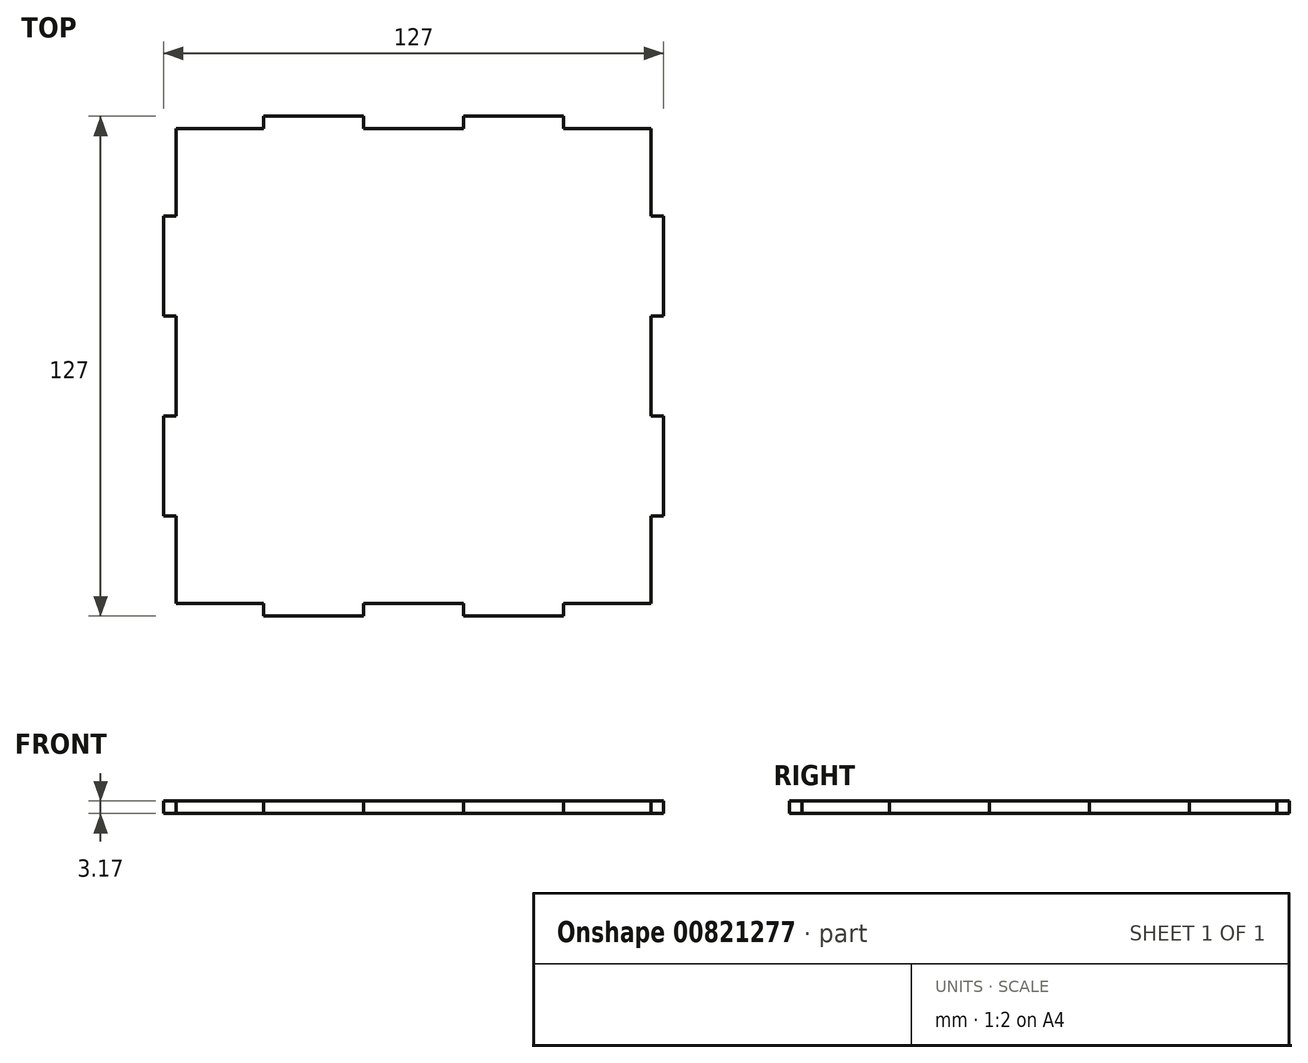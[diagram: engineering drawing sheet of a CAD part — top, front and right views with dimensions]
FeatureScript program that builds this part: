
annotation { "Feature Type Name" : "Feature", "Feature Type Description" : "" }
export const myFeature = defineFeature(function(context is Context, id is Id, definition is map)
    precondition{}
    {
        {
            var Q0;
            Q0=qCreatedBy(makeId("Top.planeOp"),FACE);
            var sketch = newSketch(context, id + "F0", { "sketchPlane" : qUnion([Q0])});
            skLineSegment(sketch, "E0.bottom", {"start": v(-63.5, 63.5) * mm, "end": v(63.5, 63.5) * mm});
            skLineSegment(sketch, "E0.top", {"start": v(-63.5, -63.5) * mm, "end": v(63.5, -63.5) * mm});
            skLineSegment(sketch, "E0.left", {"start": v(-63.5, 63.5) * mm, "end": v(-63.5, -63.5) * mm});
            skLineSegment(sketch, "E0.right", {"start": v(63.5, 63.5) * mm, "end": v(63.5, -63.5) * mm});
            skPoint(sketch, "E0.middle", {"position": v(0, 0) * mm});
            skLineSegment(sketch, "E1", {"start": v(-38.1, 63.5) * mm, "end": v(-38.1, -63.5) * mm});
            skLineSegment(sketch, "E2", {"start": v(-63.5, -38.1) * mm, "end": v(63.5, -38.1) * mm});
            skLineSegment(sketch, "E3.1.0.0", {"start": v(-12.7, 63.5) * mm, "end": v(-12.7, -63.5) * mm});
            skLineSegment(sketch, "E3.2.0.0", {"start": v(12.7, 63.5) * mm, "end": v(12.7, -63.5) * mm});
            skLineSegment(sketch, "E3.3.0.0", {"start": v(38.1, 63.5) * mm, "end": v(38.1, -63.5) * mm});
            skLineSegment(sketch, "E3.direction1", {"start": v(-38.1, -63.5) * mm, "end": v(-12.7, -63.5) * mm, "construction": true});
            skLineSegment(sketch, "E4.0.1.0", {"start": v(-63.5, -12.7) * mm, "end": v(63.5, -12.7) * mm});
            skLineSegment(sketch, "E4.0.2.0", {"start": v(-63.5, 12.7) * mm, "end": v(63.5, 12.7) * mm});
            skLineSegment(sketch, "E4.0.3.0", {"start": v(-63.5, 38.1) * mm, "end": v(63.5, 38.1) * mm});
            skLineSegment(sketch, "E4.1.0.0", {"start": v(-38.1, -38.1) * mm, "end": v(63.5, -38.1) * mm});
            skLineSegment(sketch, "E4.1.1.0", {"start": v(-38.1, -12.7) * mm, "end": v(63.5, -12.7) * mm});
            skLineSegment(sketch, "E4.1.2.0", {"start": v(-38.1, 12.7) * mm, "end": v(63.5, 12.7) * mm});
            skLineSegment(sketch, "E4.1.3.0", {"start": v(-38.1, 38.1) * mm, "end": v(63.5, 38.1) * mm});
            skLineSegment(sketch, "E4.2.0.0", {"start": v(-12.7, -38.1) * mm, "end": v(63.5, -38.1) * mm});
            skLineSegment(sketch, "E4.2.1.0", {"start": v(-12.7, -12.7) * mm, "end": v(63.5, -12.7) * mm});
            skLineSegment(sketch, "E4.2.2.0", {"start": v(-12.7, 12.7) * mm, "end": v(63.5, 12.7) * mm});
            skLineSegment(sketch, "E4.2.3.0", {"start": v(-12.7, 38.1) * mm, "end": v(63.5, 38.1) * mm});
            skLineSegment(sketch, "E4.direction1", {"start": v(-63.5, -38.1) * mm, "end": v(-38.1, -38.1) * mm, "construction": true});
            skLineSegment(sketch, "E4.direction2", {"start": v(-63.5, -38.1) * mm, "end": v(-63.5, -12.7) * mm, "construction": true});
            skLineSegment(sketch, "E5", {"start": v(-63.5, -60.33) * mm, "end": v(63.5, -60.32) * mm});
            skLineSegment(sketch, "E6", {"start": v(-60.33, 63.5) * mm, "end": v(-60.33, -63.5) * mm});
            skLineSegment(sketch, "E7", {"start": v(-63.5, 60.33) * mm, "end": v(63.5, 60.33) * mm});
            skLineSegment(sketch, "E8", {"start": v(60.32, 63.5) * mm, "end": v(60.32, -63.5) * mm});
            skSolve(sketch);
        }
        {
            var Q0;
            {var subQ0=sQuery(id+"F0.wireOp",EDGE,"E7");var subQ1=sQuery(id+"F0.wireOp",EDGE,"E1");var subQ2=makeQuery(id+"F0.imprint","INTERSECT",VERTEX,{"derivedFrom":[subQ1,subQ0]});Q0=makeQuery(id+"F0.imprint","IMPRINT",FACE,{"disambiguationData":[TD([[makeQuery(id+"F0.imprint","IMPRINT",EDGE,{"disambiguationData":[TD([[subQ2,-1.0]])],"derivedFrom":subQ1}),-1.0]])]});}
            var Q1;
            {var subQ0=sQuery(id+"F0.wireOp",EDGE,"E7");var subQ1=sQuery(id+"F0.wireOp",EDGE,"E1");var subQ2=makeQuery(id+"F0.imprint","INTERSECT",VERTEX,{"derivedFrom":[subQ1,subQ0]});Q1=makeQuery(id+"F0.imprint","IMPRINT",FACE,{"disambiguationData":[TD([[makeQuery(id+"F0.imprint","IMPRINT",EDGE,{"disambiguationData":[TD([[subQ2,-1.0]])],"derivedFrom":subQ1}),1.0]])]});}
            var Q2;
            {var subQ0=sQuery(id+"F0.wireOp",EDGE,"E7");var subQ1=sQuery(id+"F0.wireOp",EDGE,"E3.2.0.0");var subQ2=makeQuery(id+"F0.imprint","INTERSECT",VERTEX,{"derivedFrom":[subQ1,subQ0]});Q2=makeQuery(id+"F0.imprint","IMPRINT",FACE,{"disambiguationData":[TD([[makeQuery(id+"F0.imprint","IMPRINT",EDGE,{"disambiguationData":[TD([[subQ2,-1.0]])],"derivedFrom":subQ1}),1.0]])]});}
            var Q3;
            {var subQ0=sQuery(id+"F0.wireOp",EDGE,"E7");var subQ1=sQuery(id+"F0.wireOp",EDGE,"E3.3.0.0");var subQ2=makeQuery(id+"F0.imprint","INTERSECT",VERTEX,{"derivedFrom":[subQ1,subQ0]});Q3=makeQuery(id+"F0.imprint","IMPRINT",FACE,{"disambiguationData":[TD([[makeQuery(id+"F0.imprint","IMPRINT",EDGE,{"disambiguationData":[TD([[subQ2,-1.0]])],"derivedFrom":subQ1}),1.0]])]});}
            var Q4;
            {var subQ0=sQuery(id+"F0.wireOp",EDGE,"E4.0.2.0");var subQ1=sQuery(id+"F0.wireOp",EDGE,"E3.3.0.0");var subQ2=makeQuery(id+"F0.imprint","INTERSECT",VERTEX,{"derivedFrom":[subQ1,subQ0]});Q4=makeQuery(id+"F0.imprint","IMPRINT",FACE,{"disambiguationData":[TD([[makeQuery(id+"F0.imprint","IMPRINT",EDGE,{"disambiguationData":[TD([[subQ2,1.0]])],"derivedFrom":subQ1}),1.0]])]});}
            var Q5;
            {var subQ0=sQuery(id+"F0.wireOp",EDGE,"E4.0.2.0");var subQ1=sQuery(id+"F0.wireOp",EDGE,"E3.2.0.0");var subQ2=makeQuery(id+"F0.imprint","INTERSECT",VERTEX,{"derivedFrom":[subQ1,subQ0]});Q5=makeQuery(id+"F0.imprint","IMPRINT",FACE,{"disambiguationData":[TD([[makeQuery(id+"F0.imprint","IMPRINT",EDGE,{"disambiguationData":[TD([[subQ2,1.0]])],"derivedFrom":subQ1}),1.0]])]});}
            var Q6;
            {var subQ0=sQuery(id+"F0.wireOp",EDGE,"E4.0.2.0");var subQ1=sQuery(id+"F0.wireOp",EDGE,"E3.1.0.0");var subQ2=makeQuery(id+"F0.imprint","INTERSECT",VERTEX,{"derivedFrom":[subQ1,subQ0]});Q6=makeQuery(id+"F0.imprint","IMPRINT",FACE,{"disambiguationData":[TD([[makeQuery(id+"F0.imprint","IMPRINT",EDGE,{"disambiguationData":[TD([[subQ2,1.0]])],"derivedFrom":subQ1}),1.0]])]});}
            var Q7;
            {var subQ0=sQuery(id+"F0.wireOp",EDGE,"E4.0.2.0");var subQ1=sQuery(id+"F0.wireOp",EDGE,"E1");var subQ2=makeQuery(id+"F0.imprint","INTERSECT",VERTEX,{"derivedFrom":[subQ1,subQ0]});Q7=makeQuery(id+"F0.imprint","IMPRINT",FACE,{"disambiguationData":[TD([[makeQuery(id+"F0.imprint","IMPRINT",EDGE,{"disambiguationData":[TD([[subQ2,1.0]])],"derivedFrom":subQ1}),1.0]])]});}
            var Q8;
            {var subQ0=sQuery(id+"F0.wireOp",EDGE,"E4.0.2.0");var subQ1=sQuery(id+"F0.wireOp",EDGE,"E1");var subQ2=makeQuery(id+"F0.imprint","INTERSECT",VERTEX,{"derivedFrom":[subQ1,subQ0]});Q8=makeQuery(id+"F0.imprint","IMPRINT",FACE,{"disambiguationData":[TD([[makeQuery(id+"F0.imprint","IMPRINT",EDGE,{"disambiguationData":[TD([[subQ2,1.0]])],"derivedFrom":subQ1}),-1.0]])]});}
            var Q9;
            {var subQ0=sQuery(id+"F0.wireOp",EDGE,"E4.0.2.0");var subQ1=sQuery(id+"F0.wireOp",EDGE,"E1");var subQ2=makeQuery(id+"F0.imprint","INTERSECT",VERTEX,{"derivedFrom":[subQ1,subQ0]});Q9=makeQuery(id+"F0.imprint","IMPRINT",FACE,{"disambiguationData":[TD([[makeQuery(id+"F0.imprint","IMPRINT",EDGE,{"disambiguationData":[TD([[subQ2,-1.0]])],"derivedFrom":subQ1}),-1.0]])]});}
            var Q10;
            {var subQ0=sQuery(id+"F0.wireOp",EDGE,"E4.0.2.0");var subQ1=sQuery(id+"F0.wireOp",EDGE,"E1");var subQ2=makeQuery(id+"F0.imprint","INTERSECT",VERTEX,{"derivedFrom":[subQ1,subQ0]});Q10=makeQuery(id+"F0.imprint","IMPRINT",FACE,{"disambiguationData":[TD([[makeQuery(id+"F0.imprint","IMPRINT",EDGE,{"disambiguationData":[TD([[subQ2,-1.0]])],"derivedFrom":subQ1}),1.0]])]});}
            var Q11;
            {var subQ0=sQuery(id+"F0.wireOp",EDGE,"E4.0.1.0");var subQ1=sQuery(id+"F0.wireOp",EDGE,"E3.1.0.0");var subQ2=makeQuery(id+"F0.imprint","INTERSECT",VERTEX,{"derivedFrom":[subQ1,subQ0]});Q11=makeQuery(id+"F0.imprint","IMPRINT",FACE,{"disambiguationData":[TD([[makeQuery(id+"F0.imprint","IMPRINT",EDGE,{"disambiguationData":[TD([[subQ2,1.0]])],"derivedFrom":subQ1}),1.0]])]});}
            var Q12;
            {var subQ0=sQuery(id+"F0.wireOp",EDGE,"E4.0.1.0");var subQ1=sQuery(id+"F0.wireOp",EDGE,"E3.2.0.0");var subQ2=makeQuery(id+"F0.imprint","INTERSECT",VERTEX,{"derivedFrom":[subQ1,subQ0]});Q12=makeQuery(id+"F0.imprint","IMPRINT",FACE,{"disambiguationData":[TD([[makeQuery(id+"F0.imprint","IMPRINT",EDGE,{"disambiguationData":[TD([[subQ2,1.0]])],"derivedFrom":subQ1}),1.0]])]});}
            var Q13;
            {var subQ0=sQuery(id+"F0.wireOp",EDGE,"E4.0.1.0");var subQ1=sQuery(id+"F0.wireOp",EDGE,"E3.3.0.0");var subQ2=makeQuery(id+"F0.imprint","INTERSECT",VERTEX,{"derivedFrom":[subQ1,subQ0]});Q13=makeQuery(id+"F0.imprint","IMPRINT",FACE,{"disambiguationData":[TD([[makeQuery(id+"F0.imprint","IMPRINT",EDGE,{"disambiguationData":[TD([[subQ2,1.0]])],"derivedFrom":subQ1}),1.0]])]});}
            var Q14;
            {var subQ0=sQuery(id+"F0.wireOp",EDGE,"E3.3.0.0");var subQ1=sQuery(id+"F0.wireOp",EDGE,"E2");var subQ2=makeQuery(id+"F0.imprint","INTERSECT",VERTEX,{"derivedFrom":[subQ1,subQ0]});Q14=makeQuery(id+"F0.imprint","IMPRINT",FACE,{"disambiguationData":[TD([[makeQuery(id+"F0.imprint","IMPRINT",EDGE,{"disambiguationData":[TD([[subQ2,-1.0]])],"derivedFrom":subQ1}),1.0]])]});}
            var Q15;
            {var subQ0=sQuery(id+"F0.wireOp",EDGE,"E3.2.0.0");var subQ1=sQuery(id+"F0.wireOp",EDGE,"E2");var subQ2=makeQuery(id+"F0.imprint","INTERSECT",VERTEX,{"derivedFrom":[subQ1,subQ0]});Q15=makeQuery(id+"F0.imprint","IMPRINT",FACE,{"disambiguationData":[TD([[makeQuery(id+"F0.imprint","IMPRINT",EDGE,{"disambiguationData":[TD([[subQ2,-1.0]])],"derivedFrom":subQ1}),1.0]])]});}
            var Q16;
            {var subQ0=sQuery(id+"F0.wireOp",EDGE,"E3.1.0.0");var subQ1=sQuery(id+"F0.wireOp",EDGE,"E2");var subQ2=makeQuery(id+"F0.imprint","INTERSECT",VERTEX,{"derivedFrom":[subQ1,subQ0]});Q16=makeQuery(id+"F0.imprint","IMPRINT",FACE,{"disambiguationData":[TD([[makeQuery(id+"F0.imprint","IMPRINT",EDGE,{"disambiguationData":[TD([[subQ2,-1.0]])],"derivedFrom":subQ1}),1.0]])]});}
            var Q17;
            {var subQ0=sQuery(id+"F0.wireOp",EDGE,"E4.0.1.0");var subQ1=sQuery(id+"F0.wireOp",EDGE,"E1");var subQ2=makeQuery(id+"F0.imprint","INTERSECT",VERTEX,{"derivedFrom":[subQ1,subQ0]});Q17=makeQuery(id+"F0.imprint","IMPRINT",FACE,{"disambiguationData":[TD([[makeQuery(id+"F0.imprint","IMPRINT",EDGE,{"disambiguationData":[TD([[subQ2,-1.0]])],"derivedFrom":subQ1}),1.0]])]});}
            var Q18;
            {var subQ0=sQuery(id+"F0.wireOp",EDGE,"E4.0.1.0");var subQ1=sQuery(id+"F0.wireOp",EDGE,"E1");var subQ2=makeQuery(id+"F0.imprint","INTERSECT",VERTEX,{"derivedFrom":[subQ1,subQ0]});Q18=makeQuery(id+"F0.imprint","IMPRINT",FACE,{"disambiguationData":[TD([[makeQuery(id+"F0.imprint","IMPRINT",EDGE,{"disambiguationData":[TD([[subQ2,-1.0]])],"derivedFrom":subQ1}),-1.0]])]});}
            var Q19;
            {var subQ0=sQuery(id+"F0.wireOp",EDGE,"E5");var subQ1=sQuery(id+"F0.wireOp",EDGE,"E1");var subQ2=makeQuery(id+"F0.imprint","INTERSECT",VERTEX,{"derivedFrom":[subQ1,subQ0]});Q19=makeQuery(id+"F0.imprint","IMPRINT",FACE,{"disambiguationData":[TD([[makeQuery(id+"F0.imprint","IMPRINT",EDGE,{"disambiguationData":[TD([[subQ2,1.0]])],"derivedFrom":subQ1}),-1.0]])]});}
            var Q20;
            {var subQ0=sQuery(id+"F0.wireOp",EDGE,"E5");var subQ1=sQuery(id+"F0.wireOp",EDGE,"E1");var subQ2=makeQuery(id+"F0.imprint","INTERSECT",VERTEX,{"derivedFrom":[subQ1,subQ0]});Q20=makeQuery(id+"F0.imprint","IMPRINT",FACE,{"disambiguationData":[TD([[makeQuery(id+"F0.imprint","IMPRINT",EDGE,{"disambiguationData":[TD([[subQ2,1.0]])],"derivedFrom":subQ1}),1.0]])]});}
            var Q21;
            {var subQ0=sQuery(id+"F0.wireOp",EDGE,"E3.2.0.0");var subQ1=sQuery(id+"F0.wireOp",EDGE,"E2");var subQ2=makeQuery(id+"F0.imprint","INTERSECT",VERTEX,{"derivedFrom":[subQ1,subQ0]});Q21=makeQuery(id+"F0.imprint","IMPRINT",FACE,{"disambiguationData":[TD([[makeQuery(id+"F0.imprint","IMPRINT",EDGE,{"disambiguationData":[TD([[subQ2,-1.0]])],"derivedFrom":subQ1}),-1.0]])]});}
            var Q22;
            {var subQ0=sQuery(id+"F0.wireOp",EDGE,"E3.3.0.0");var subQ1=sQuery(id+"F0.wireOp",EDGE,"E2");var subQ2=makeQuery(id+"F0.imprint","INTERSECT",VERTEX,{"derivedFrom":[subQ1,subQ0]});Q22=makeQuery(id+"F0.imprint","IMPRINT",FACE,{"disambiguationData":[TD([[makeQuery(id+"F0.imprint","IMPRINT",EDGE,{"disambiguationData":[TD([[subQ2,-1.0]])],"derivedFrom":subQ1}),-1.0]])]});}
            var Q23;
            {var subQ0=sQuery(id+"F0.wireOp",EDGE,"E7");var subQ1=sQuery(id+"F0.wireOp",EDGE,"E3.1.0.0");var subQ2=makeQuery(id+"F0.imprint","INTERSECT",VERTEX,{"derivedFrom":[subQ1,subQ0]});Q23=makeQuery(id+"F0.imprint","IMPRINT",FACE,{"disambiguationData":[TD([[makeQuery(id+"F0.imprint","IMPRINT",EDGE,{"disambiguationData":[TD([[subQ2,-1.0]])],"derivedFrom":subQ1}),1.0]])]});}
            var Q24;
            {var subQ0=sQuery(id+"F0.wireOp",EDGE,"E3.1.0.0");var subQ1=sQuery(id+"F0.wireOp",EDGE,"E2");var subQ2=makeQuery(id+"F0.imprint","INTERSECT",VERTEX,{"derivedFrom":[subQ1,subQ0]});Q24=makeQuery(id+"F0.imprint","IMPRINT",FACE,{"disambiguationData":[TD([[makeQuery(id+"F0.imprint","IMPRINT",EDGE,{"disambiguationData":[TD([[subQ2,-1.0]])],"derivedFrom":subQ1}),-1.0]])]});}
            var Q25;
            {var subQ0=sQuery(id+"F0.wireOp",EDGE,"E3.1.0.0");var subQ1=sQuery(id+"F0.wireOp",EDGE,"E0.top");var subQ2=makeQuery(id+"F0.imprint","INTERSECT",VERTEX,{"derivedFrom":[subQ1,subQ0]});Q25=makeQuery(id+"F0.imprint","IMPRINT",FACE,{"disambiguationData":[TD([[makeQuery(id+"F0.imprint","IMPRINT",EDGE,{"disambiguationData":[TD([[subQ2,1.0]])],"derivedFrom":subQ1}),1.0]])]});}
            var Q26;
            {var subQ0=sQuery(id+"F0.wireOp",EDGE,"E4.0.1.0");var subQ1=sQuery(id+"F0.wireOp",EDGE,"E0.left");var subQ2=makeQuery(id+"F0.imprint","INTERSECT",VERTEX,{"derivedFrom":[subQ1,subQ0]});Q26=makeQuery(id+"F0.imprint","IMPRINT",FACE,{"disambiguationData":[TD([[makeQuery(id+"F0.imprint","IMPRINT",EDGE,{"disambiguationData":[TD([[subQ2,-1.0]])],"derivedFrom":subQ1}),1.0]])]});}
            var Q27;
            {var subQ0=sQuery(id+"F0.wireOp",EDGE,"E4.0.2.0");var subQ1=sQuery(id+"F0.wireOp",EDGE,"E0.left");var subQ2=makeQuery(id+"F0.imprint","INTERSECT",VERTEX,{"derivedFrom":[subQ1,subQ0]});Q27=makeQuery(id+"F0.imprint","IMPRINT",FACE,{"disambiguationData":[TD([[makeQuery(id+"F0.imprint","IMPRINT",EDGE,{"disambiguationData":[TD([[subQ2,1.0]])],"derivedFrom":subQ1}),1.0]])]});}
            var Q28;
            {var subQ0=sQuery(id+"F0.wireOp",EDGE,"E1");var subQ1=sQuery(id+"F0.wireOp",EDGE,"E0.bottom");var subQ2=makeQuery(id+"F0.imprint","INTERSECT",VERTEX,{"derivedFrom":[subQ1,subQ0]});Q28=makeQuery(id+"F0.imprint","IMPRINT",FACE,{"disambiguationData":[TD([[makeQuery(id+"F0.imprint","IMPRINT",EDGE,{"disambiguationData":[TD([[subQ2,-1.0]])],"derivedFrom":subQ1}),-1.0]])]});}
            var Q29;
            {var subQ0=sQuery(id+"F0.wireOp",EDGE,"E3.2.0.0");var subQ1=sQuery(id+"F0.wireOp",EDGE,"E0.bottom");var subQ2=makeQuery(id+"F0.imprint","INTERSECT",VERTEX,{"derivedFrom":[subQ1,subQ0]});Q29=makeQuery(id+"F0.imprint","IMPRINT",FACE,{"disambiguationData":[TD([[makeQuery(id+"F0.imprint","IMPRINT",EDGE,{"disambiguationData":[TD([[subQ2,-1.0]])],"derivedFrom":subQ1}),-1.0]])]});}
            var Q30;
            {var subQ0=sQuery(id+"F0.wireOp",EDGE,"E4.0.2.0");var subQ1=sQuery(id+"F0.wireOp",EDGE,"E0.right");var subQ2=makeQuery(id+"F0.imprint","INTERSECT",VERTEX,{"derivedFrom":[subQ1,subQ0]});Q30=makeQuery(id+"F0.imprint","IMPRINT",FACE,{"disambiguationData":[TD([[makeQuery(id+"F0.imprint","IMPRINT",EDGE,{"disambiguationData":[TD([[subQ2,1.0]])],"derivedFrom":subQ1}),-1.0]])]});}
            var Q31;
            {var subQ0=sQuery(id+"F0.wireOp",EDGE,"E4.0.1.0");var subQ1=sQuery(id+"F0.wireOp",EDGE,"E0.right");var subQ2=makeQuery(id+"F0.imprint","INTERSECT",VERTEX,{"derivedFrom":[subQ1,subQ0]});Q31=makeQuery(id+"F0.imprint","IMPRINT",FACE,{"disambiguationData":[TD([[makeQuery(id+"F0.imprint","IMPRINT",EDGE,{"disambiguationData":[TD([[subQ2,-1.0]])],"derivedFrom":subQ1}),-1.0]])]});}
            var Q32;
            {var subQ0=sQuery(id+"F0.wireOp",EDGE,"E3.2.0.0");var subQ1=sQuery(id+"F0.wireOp",EDGE,"E0.top");var subQ2=makeQuery(id+"F0.imprint","INTERSECT",VERTEX,{"derivedFrom":[subQ1,subQ0]});Q32=makeQuery(id+"F0.imprint","IMPRINT",FACE,{"disambiguationData":[TD([[makeQuery(id+"F0.imprint","IMPRINT",EDGE,{"disambiguationData":[TD([[subQ2,-1.0]])],"derivedFrom":subQ1}),1.0]])]});}
            extrude(context, id + "F1", {"entities" : qUnion([Q0, Q1, Q2, Q3, Q4, Q5, Q6, Q7, Q8, Q9, Q10, Q11, Q12, Q13, Q14, Q15, Q16, Q17, Q18, Q19, Q20, Q21, Q22, Q23, Q24, Q25, Q26, Q27, Q28, Q29, Q30, Q31, Q32]), "depth" : 3.17 * mm, "offsetDistance" : 25.4 * mm});
        }
    });
